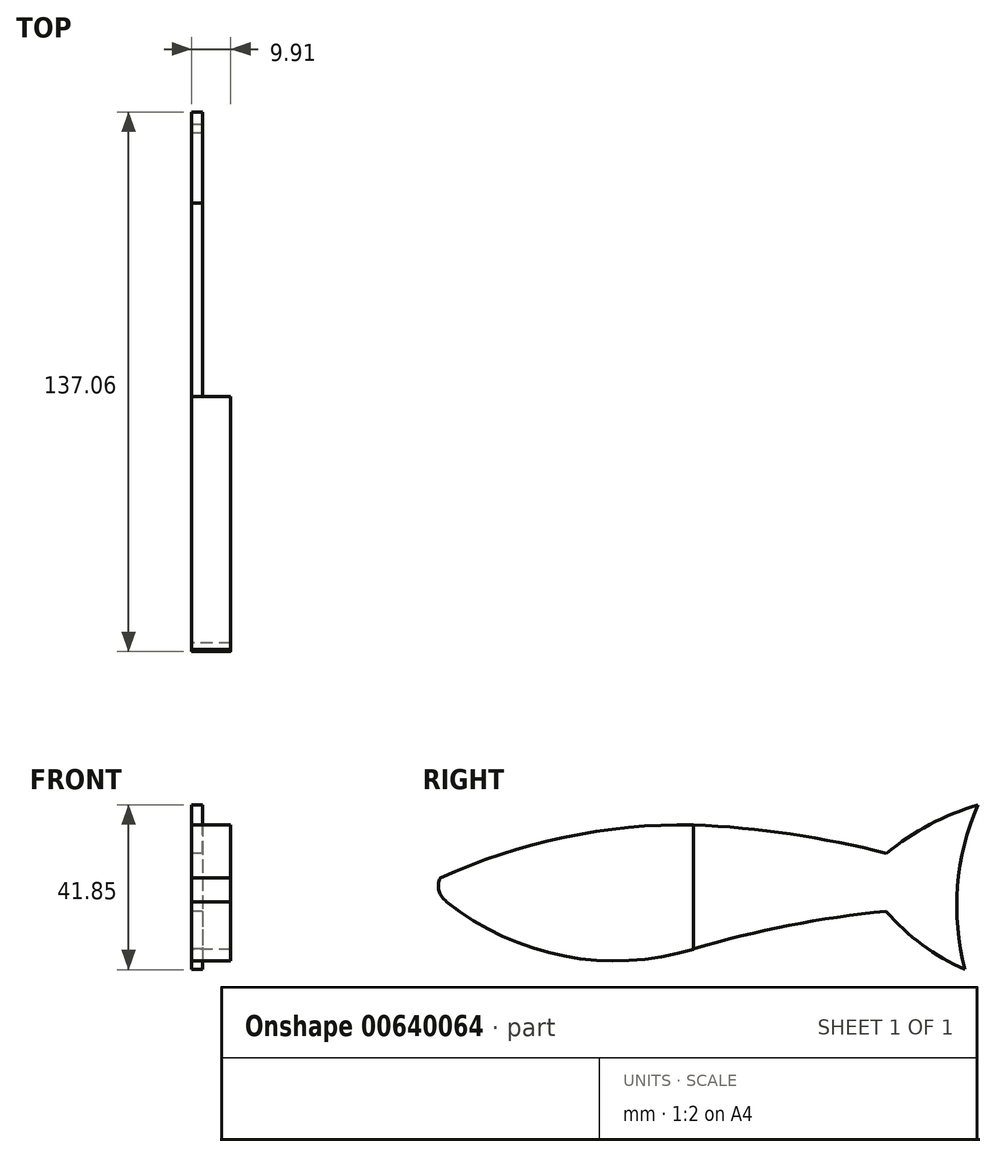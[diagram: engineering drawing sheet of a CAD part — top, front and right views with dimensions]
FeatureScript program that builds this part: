
annotation { "Feature Type Name" : "Feature", "Feature Type Description" : "" }
export const myFeature = defineFeature(function(context is Context, id is Id, definition is map)
    precondition{}
    {
        {
            var Q0;
            Q0=qCreatedBy(makeId("Right.planeOp"),FACE);
            var sketch = newSketch(context, id + "F0", { "sketchPlane" : qUnion([Q0])});
            skLineSegment(sketch, "E0", {"start": v(0, 15.7) * mm, "end": v(0, -15.93) * mm});
            skArc(sketch, "E1", {"start": v(0, 15.7) * mm, "mid": v(-32.9, 12.5) * mm, "end": v(-64.31, 2.2) * mm});
            skArc(sketch, "E2", {"start": v(-62.68, -3.84) * mm, "mid": v(-32.84, -17.67) * mm, "end": v(0, -15.93) * mm});
            skArc(sketch, "E3", {"start": v(-64.31, 2.2) * mm, "mid": v(-64.66, -1.13) * mm, "end": v(-62.68, -3.84) * mm});
            skSolve(sketch);
        }
        {
            var Q0;
            Q0=makeQuery(id+"F0.imprint","IMPRINT",FACE,{"disambiguationData":[TD([[makeQuery(id+"F0.imprint","IMPRINT",EDGE,{"derivedFrom":sQuery(id+"F0.wireOp",EDGE,"E0")}),-1.0]])]});
            extrude(context, id + "F1", {"entities" : qUnion([Q0]), "depth" : 9.9 * mm, "offsetDistance" : 25.4 * mm});
        }
        {
            var Q0;
            Q0=qCreatedBy(makeId("Right.planeOp"),FACE);
            var sketch = newSketch(context, id + "F2", { "sketchPlane" : qUnion([Q0])});
            skArc(sketch, "E4", {"start": v(49.04, 8.45) * mm, "mid": v(24.7, 13.31) * mm, "end": v(0, 15.7) * mm});
            skArc(sketch, "E5", {"start": v(48.94, -6.28) * mm, "mid": v(24.24, -9.89) * mm, "end": v(0, -15.86) * mm});
            skArc(sketch, "E6", {"start": v(72.24, 20.74) * mm, "mid": v(60.04, 15.73) * mm, "end": v(49.04, 8.45) * mm});
            skArc(sketch, "E7", {"start": v(72.24, 20.74) * mm, "mid": v(67.1, 0.09) * mm, "end": v(69, -21.1) * mm});
            skArc(sketch, "E8", {"start": v(48.94, -6.28) * mm, "mid": v(58.15, -14.81) * mm, "end": v(69, -21.1) * mm});
            skLineSegment(sketch, "E9", {"start": v(0, 15.7) * mm, "end": v(0, -15.86) * mm});
            skSolve(sketch);
        }
        {
            var Q0;
            Q0 = qSketchRegion(id + "F2", true);
            extrude(context, id + "F3", {"entities" : qUnion([Q0]), "operationType" : NewBodyOperationType.ADD, "depth" : 2.8 * mm, "offsetDistance" : 25.4 * mm});
        }
    });
